# Revit family: Стол медицинский без тумбы ДМ
name_source: partatom
category: Оборудование
revit_build: Autodesk Revit 2017 (Build: 20170118_1100(x64)
units: mm (PartAtom-declared; Revit-internal decimal feet)

## family parameters
Всегда вертикально = Да
На основе рабочей плоскости = Нет
Общий = Нет
При загрузке вырезать с полостями = Нет
Размер круглого соединителя = Использовать диаметр
Тип детали = Нормальный
Точка расчета площади = Нет

## types (3) — shared parameters
Длина ручек = 150 мм
Каркас = Алюминий 7075
Ножки = Пластмасса, непрозрачная, черная
Общ_Высота = 820 мм
Общ_Глубина = 600 мм
Общ_Единицы измерения = шт.
Общ_Наименование = Стол медицинский без тумбы
Общ_Поставщик = Доктор Мебель
Панели = Пластмасса, непрозрачная, белая
Ручки = Алюминий 7075
Фасад = Столешница медицинской мебели ДСП с пластиковым покрытием

## per-type parameters (varying)
| type | Общ_Тип, марка | Общ_Ширина |
| 900х600 | ДМ-2-006-01 | 900 мм |
| 1200х600 | ДМ-2-006-02 | 1200 мм |
| 1500х600 | ДМ-2-006-03 | 1500 мм |
